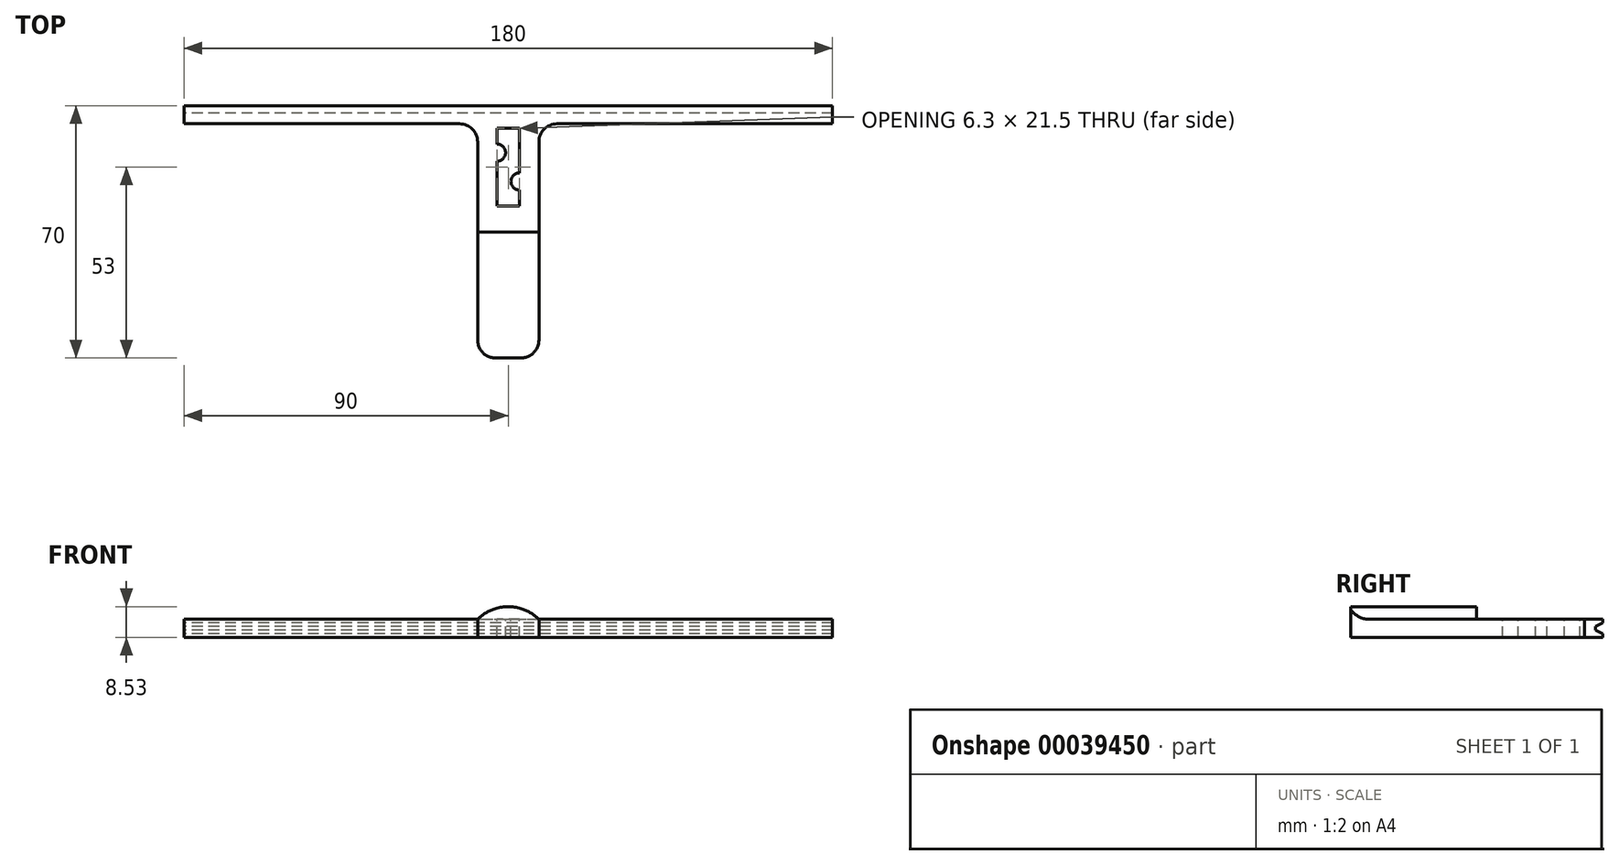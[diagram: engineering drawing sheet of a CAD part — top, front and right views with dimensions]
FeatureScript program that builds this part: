
annotation { "Feature Type Name" : "Feature", "Feature Type Description" : "" }
export const myFeature = defineFeature(function(context is Context, id is Id, definition is map)
    precondition{}
    {
        {
            var Q0;
            Q0=qCreatedBy(makeId("Top.planeOp"),FACE);
            var sketch = newSketch(context, id + "F0", { "sketchPlane" : qUnion([Q0])});
            skLineSegment(sketch, "E0", {"start": v(0, 35) * mm, "end": v(0, -35) * mm, "construction": true});
            skLineSegment(sketch, "E1", {"start": v(-8.5, -40) * mm, "end": v(-8.5, -110) * mm});
            skLineSegment(sketch, "E2", {"start": v(-8.5, -110) * mm, "end": v(0, -110) * mm});
            skLineSegment(sketch, "E3.MirrorCS", {"start": v(8.5, -40) * mm, "end": v(8.5, -110) * mm});
            skLineSegment(sketch, "E4.MirrorCS", {"start": v(8.5, -110) * mm, "end": v(0, -110) * mm});
            skEllipse(sketch, "E5.0", {"center": v(0, 0) * mm, "majorRadius": 67.5 * mm, "minorRadius": 35 * mm, "majorAxis": v(1, 0), "construction": true});
            skCircle(sketch, "E6.0", {"center": v(-32, 0) * mm, "radius": 17.5 * mm, "construction": true});
            skCircle(sketch, "E7.0", {"center": v(32, 0) * mm, "radius": 17.5 * mm, "construction": true});
            skLineSegment(sketch, "E8", {"start": v(0, -110) * mm, "end": v(0, -40) * mm, "construction": true});
            skLineSegment(sketch, "E9", {"start": v(0, -35) * mm, "end": v(0, -40) * mm, "construction": true});
            skLineSegment(sketch, "E10", {"start": v(-8.5, -40) * mm, "end": v(8.5, -40) * mm});
            skSolve(sketch);
        }
        {
            var Q0;
            Q0=qSketchRegion(id+"F0",true);
            extrude(context, id + "F1", {"entities" : qUnion([Q0]), "depth" : 5 * mm});
        }
        {
            var Q0;
            Q0=makeQuery(id+"F1.opExtrude","CAP_FACE",FACE,{"disambiguationData":[OSD([sQuery(id+"F0.wireOp",EDGE,"7391e9a9-ae98-415e-9696-a7713fd930ae"),sQuery(id+"F0.wireOp",EDGE,"7767e17a-6af5-4bc8-a544-19a58f6916b8"),sQuery(id+"F0.wireOp",EDGE,"E1"),sQuery(id+"F0.wireOp",EDGE,"E2"),sQuery(id+"F0.wireOp",EDGE,"69639bf5-fd83-4191-99ff-23f08a1ee2360.MirrorCS"),sQuery(id+"F0.wireOp",EDGE,"e829f9c4-7dbb-4f23-9f44-d63990e1826a0.MirrorCS"),sQuery(id+"F0.wireOp",EDGE,"E3.MirrorCS"),sQuery(id+"F0.wireOp",EDGE,"E4.MirrorCS")])],"isStart":false});
            var sketch = newSketch(context, id + "F2", { "sketchPlane" : qUnion([Q0])});
            skLineSegment(sketch, "E11", {"start": v(0, 0) * mm, "end": v(0, -57) * mm, "construction": true});
            skLineSegment(sketch, "E12.rect.bottom", {"start": v(3.15, -67.75) * mm, "end": v(-3.15, -67.75) * mm});
            skLineSegment(sketch, "E12.rect.top", {"start": v(3.15, -46.25) * mm, "end": v(-3.15, -46.25) * mm});
            skLineSegment(sketch, "E12.rect.left", {"start": v(3.15, -67.75) * mm, "end": v(3.15, -46.25) * mm, "construction": true});
            skLineSegment(sketch, "E12.rect.right", {"start": v(-3.15, -67.75) * mm, "end": v(-3.15, -46.25) * mm, "construction": true});
            skPoint(sketch, "E12.rect.middle", {"position": v(0, -57) * mm});
            skLineSegment(sketch, "E13", {"start": v(-3.15, -46.25) * mm, "end": v(-3.15, -50.6) * mm});
            skArc(sketch, "E14", {"start": v(-3.15, -55.4) * mm, "mid": v(-0.75, -53) * mm, "end": v(-3.15, -50.6) * mm});
            skLineSegment(sketch, "E15", {"start": v(-3.15, -53) * mm, "end": v(-3.15, -46.25) * mm, "construction": true});
            skLineSegment(sketch, "E16", {"start": v(-3.15, -55.4) * mm, "end": v(-3.15, -67.75) * mm});
            skLineSegment(sketch, "E17", {"start": v(3.15, -67.75) * mm, "end": v(3.15, -63.4) * mm});
            skArc(sketch, "E18", {"start": v(3.15, -58.6) * mm, "mid": v(0.75, -61) * mm, "end": v(3.15, -63.4) * mm});
            skLineSegment(sketch, "E19", {"start": v(3.15, -58.6) * mm, "end": v(3.15, -46.25) * mm});
            skLineSegment(sketch, "E20", {"start": v(-3.15, -53) * mm, "end": v(-3.15, -57) * mm, "construction": true});
            skLineSegment(sketch, "E21", {"start": v(-3.15, -57) * mm, "end": v(0, -57) * mm, "construction": true});
            skLineSegment(sketch, "E22", {"start": v(3.15, -61) * mm, "end": v(3.15, -57) * mm, "construction": true});
            skSolve(sketch);
        }
        {
            var Q0;
            Q0=qSketchRegion(id+"F2",true);
            extrude(context, id + "F3", {"entities" : qUnion([Q0]), "operationType" : NewBodyOperationType.REMOVE, "endBound" : BoundingType.THROUGH_ALL, "oppositeDirection" : true, "depth" : 140 * mm});
        }
        {
            var Q0;
            Q0=makeQuery(id+"F1.opExtrude","SWEPT_FACE",FACE,{"disambiguationData":[OSD([sQuery(id+"F0.wireOp",EDGE,"E2"),sQuery(id+"F0.wireOp",EDGE,"E4.MirrorCS")])]});
            var sketch = newSketch(context, id + "F4", { "sketchPlane" : qUnion([Q0])});
            skLineSegment(sketch, "E23", {"start": v(-8.5, 5) * mm, "end": v(8.5, 5) * mm});
            skArc(sketch, "E24", {"start": v(8.5, 5) * mm, "mid": v(0, 8.53) * mm, "end": v(-8.5, 5) * mm});
            skSolve(sketch);
        }
        {
            var Q0;
            Q0=qSketchRegion(id+"F4",true);
            extrude(context, id + "F5", {"entities" : qUnion([Q0]), "operationType" : NewBodyOperationType.ADD, "oppositeDirection" : true, "depth" : 35 * mm});
        }
        {
            var Q0;
            Q0=qCreatedBy(makeId("Right.planeOp"),FACE);
            var sketch = newSketch(context, id + "F6", { "sketchPlane" : qUnion([Q0])});
            skPoint(sketch, "E25.0", {"position": v(-40, 5) * mm});
            skLineSegment(sketch, "E26.bottom", {"start": v(-40, 5) * mm, "end": v(-45, 5) * mm});
            skLineSegment(sketch, "E26.top", {"start": v(-40, 0) * mm, "end": v(-45, 0) * mm});
            skLineSegment(sketch, "E26.left", {"start": v(-40, 5) * mm, "end": v(-40, 0) * mm});
            skLineSegment(sketch, "E26.right", {"start": v(-45, 5) * mm, "end": v(-45, 0) * mm});
            skSolve(sketch);
        }
        {
            var Q0;
            Q0 = qSketchRegion(id + "F6", true);
            extrude(context, id + "F7", {"entities" : qUnion([Q0]), "operationType" : NewBodyOperationType.ADD, "depth" : 90 * mm, "hasSecondDirection" : true, "secondDirectionOppositeDirection" : true, "secondDirectionDepth" : 90 * mm});
        }
        {
            var Q0;
            Q0=makeQuery(id+"F7.opExtrude","CAP_FACE",FACE,{"disambiguationData":[OSD([sQuery(id+"F6.wireOp",EDGE,"E26.bottom"),sQuery(id+"F6.wireOp",EDGE,"E26.top"),sQuery(id+"F6.wireOp",EDGE,"E26.left"),sQuery(id+"F6.wireOp",EDGE,"E26.right")])],"isStart":true});
            var sketch = newSketch(context, id + "F8", { "sketchPlane" : qUnion([Q0])});
            skLineSegment(sketch, "E27", {"start": v(40, 0) * mm, "end": v(40, 1) * mm, "construction": true});
            skLineSegment(sketch, "E28", {"start": v(40, 1) * mm, "end": v(42, 1) * mm, "construction": true});
            skLineSegment(sketch, "E29", {"start": v(42, 1) * mm, "end": v(42, 2) * mm, "construction": true});
            skLineSegment(sketch, "E30", {"start": v(42, 2) * mm, "end": v(42, 3) * mm});
            skLineSegment(sketch, "E31", {"start": v(40, 1) * mm, "end": v(42, 2) * mm});
            skLineSegment(sketch, "E32", {"start": v(42, 3) * mm, "end": v(40, 4) * mm});
            skLineSegment(sketch, "E33", {"start": v(40, 1) * mm, "end": v(40, 4) * mm});
            skSolve(sketch);
        }
        {
            var Q0;
            Q0 = qSketchRegion(id + "F8", true);
            extrude(context, id + "F9", {"entities" : qUnion([Q0]), "operationType" : NewBodyOperationType.REMOVE, "endBound" : BoundingType.THROUGH_ALL, "oppositeDirection" : true, "depth" : 25 * mm});
        }
        {
            var Q0;
            Q0=makeQuery(id+"F5.opExtrude","CAP_EDGE",EDGE,{"disambiguationData":[OSD([sQuery(id+"F4.wireOp",EDGE,"E23")])],"isStart":false});
            var Q1;
            Q1=makeQuery(id+"F7.boolean.opBoolean","INTERSECT",EDGE,{"derivedFrom":[makeQuery(id+"F1.opExtrude","SWEPT_FACE",FACE,{"disambiguationData":[OSD([sQuery(id+"F0.wireOp",EDGE,"E1")])]}),makeQuery(id+"F7.opExtrude","SWEPT_FACE",FACE,{"disambiguationData":[OSD([sQuery(id+"F6.wireOp",EDGE,"E26.right")])]})]});
            var Q2;
            Q2=makeQuery(id+"F7.boolean.opBoolean","INTERSECT",EDGE,{"derivedFrom":[makeQuery(id+"F1.opExtrude","SWEPT_FACE",FACE,{"disambiguationData":[OSD([sQuery(id+"F0.wireOp",EDGE,"E3.MirrorCS")])]}),makeQuery(id+"F7.opExtrude","SWEPT_FACE",FACE,{"disambiguationData":[OSD([sQuery(id+"F6.wireOp",EDGE,"E26.right")])]})]});
            var Q3;
            Q3=makeQuery(id+"F1.opExtrude","SWEPT_EDGE",EDGE,{"disambiguationData":[OSD([sQuery(id+"F0.wireOp",EDGE,"E1"),sQuery(id+"F0.wireOp",EDGE,"E2")])]});
            var Q4;
            Q4=makeQuery(id+"F1.opExtrude","SWEPT_EDGE",EDGE,{"disambiguationData":[OSD([sQuery(id+"F0.wireOp",EDGE,"E3.MirrorCS"),sQuery(id+"F0.wireOp",EDGE,"E4.MirrorCS")])]});
            fillet(context, id + "F10", {"entities" : qUnion([Q0, Q1, Q2, Q3, Q4]), "radius" : 5 * mm, "tangentPropagation" : true, "allowEdgeOverflow" : false});
        }
    });
